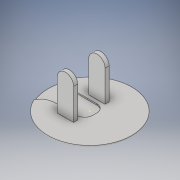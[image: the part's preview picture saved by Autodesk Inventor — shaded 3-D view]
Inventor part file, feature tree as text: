
AUTODESK INVENTOR PART (.ipt)
format: ipt  version: 2018 (Build 220112000, 112)  size: 165,376 bytes
history: native  units: in
note: dims shown in document units (in); Inventor stores cm internally (conversion verified against a paired STEP export)
features: extrude x4, sketch x3, fillet x2
ambient origin geometry x8: Origin, YZ Plane, XZ Plane, XY Plane, X Axis, Y Axis, Z Axis, Center Point
bodies: Solid1 (feature_tree)
feature tree (9):
  extrude  "Extrusion1"  Depth=0.0394in TaperAngle=0.0deg
  fillet  "Fillet1"  Radius=0.04in
  sketch  "Sketch2"  dims[d17=0.26in d18=0.065in]
  sketch  "Sketch3"  dims[d20=0.5in d21=0.26in d22=0.065in d23=0.626in d24=0.0in d25=0.626in d26=0.0in d27=0.13in d28=0.125in d29=0.0197in d30=0.0in]
  extrude  "Extrusion2"  Depth=0.065in
  extrude  "Extrusion3"  Depth=0.125in
  fillet  "Fillet2"  Radius=0.065in
  extrude  "Extrusion4"  Depth=0.125in TaperAngle=0.0deg
  sketch  "Sketch1"  dims[d0=1.332in d1=0.0394in d2=0.0in d3=0.04in]
